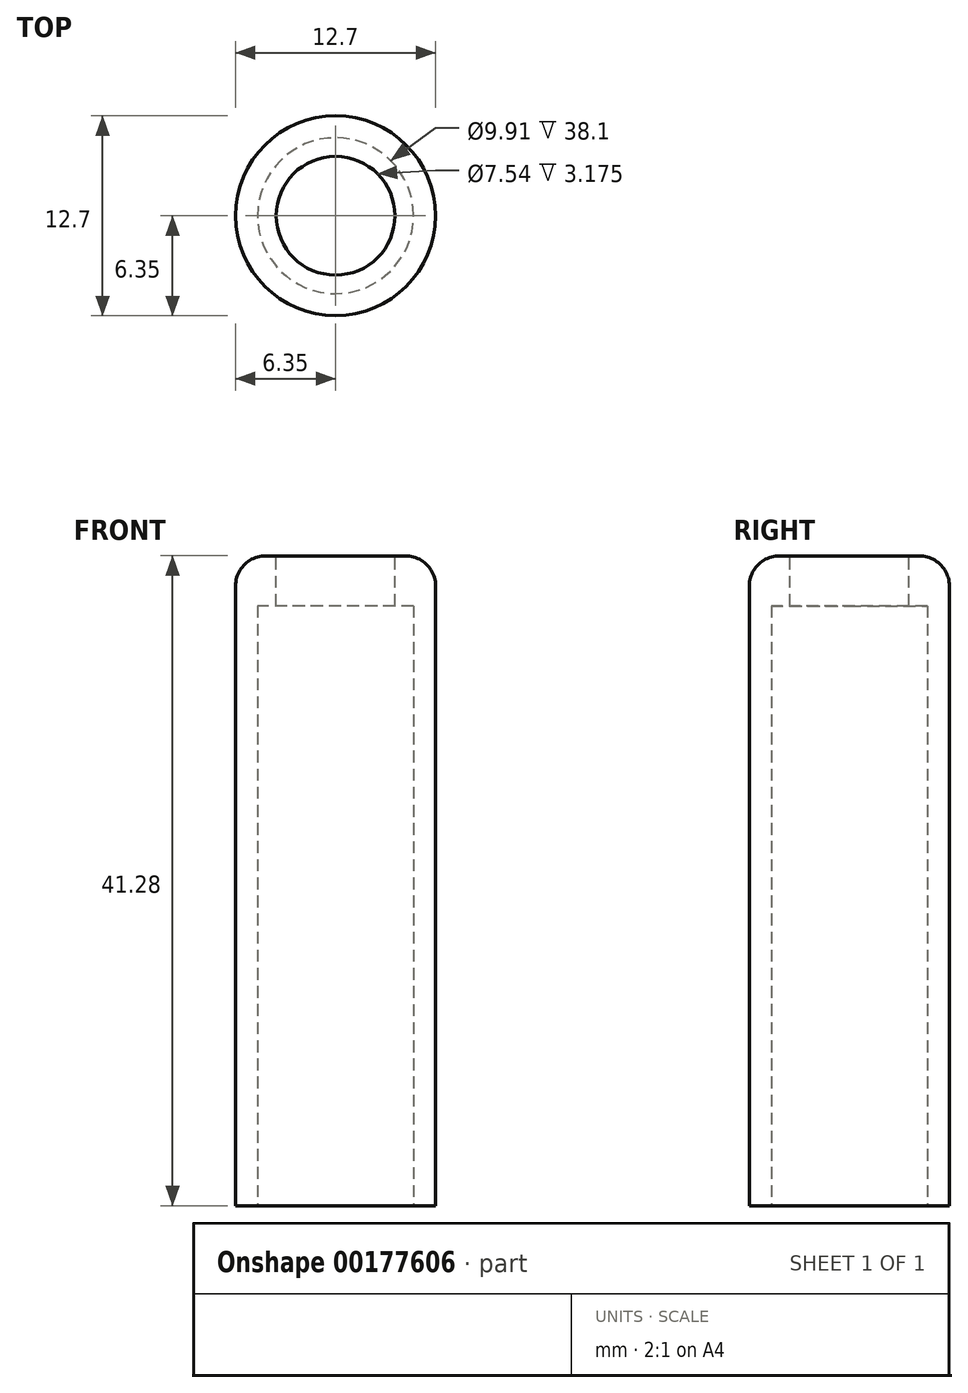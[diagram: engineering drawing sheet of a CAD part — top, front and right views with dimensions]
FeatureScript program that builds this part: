
annotation { "Feature Type Name" : "Feature", "Feature Type Description" : "" }
export const myFeature = defineFeature(function(context is Context, id is Id, definition is map)
    precondition{}
    {
        {
            var Q0;
            Q0=qCreatedBy(makeId("Top.planeOp"),FACE);
            var sketch = newSketch(context, id + "F0", { "sketchPlane" : qUnion([Q0])});
            skCircle(sketch, "E0", {"center": v(0, 0) * mm, "radius": 6.35 * mm});
            skSolve(sketch);
        }
        {
            var Q0;
            Q0=makeQuery(id+"F0.imprint","IMPRINT",FACE,{"disambiguationData":[TD([[makeQuery(id+"F0.imprint","IMPRINT",EDGE,{"derivedFrom":sQuery(id+"F0.wireOp",EDGE,"E0")}),1.0]])]});
            extrude(context, id + "F1", {"entities" : qUnion([Q0]), "depth" : 41.27 * mm});
        }
        {
            var Q0;
            Q0=qCreatedBy(makeId("Top.planeOp"),FACE);
            var sketch = newSketch(context, id + "F2", { "sketchPlane" : qUnion([Q0])});
            skCircle(sketch, "E1", {"center": v(0, 0) * mm, "radius": 4.95 * mm});
            skSolve(sketch);
        }
        {
            var Q0;
            Q0 = qSketchRegion(id + "F2", true);
            extrude(context, id + "F3", {"entities" : qUnion([Q0]), "operationType" : NewBodyOperationType.REMOVE, "depth" : 38.1 * mm});
        }
        {
            var Q0;
            Q0=makeQuery(id+"F1.opExtrude","CAP_FACE",FACE,{"disambiguationData":[OSD([sQuery(id+"F0.wireOp",EDGE,"E0")])],"isStart":false});
            cPlane(context, id + "F4", {"entities" : qUnion([Q0]), "cplaneType" : CPlaneType.OFFSET, "offset" : 0 * mm, "width" : 152.4 * mm, "height" : 152.4 * mm});
        }
        {
            var Q0;
            Q0=qCreatedBy(id+"F4.planeOp",FACE);
            var sketch = newSketch(context, id + "F5", { "sketchPlane" : qUnion([Q0])});
            skCircle(sketch, "E2", {"center": v(0, 0) * mm, "radius": 3.77 * mm});
            skSolve(sketch);
        }
        {
            var Q0;
            Q0=makeQuery(id+"F5.imprint","IMPRINT",FACE,{"disambiguationData":[TD([[makeQuery(id+"F5.imprint","IMPRINT",EDGE,{"derivedFrom":sQuery(id+"F5.wireOp",EDGE,"E2")}),1.0]])]});
            extrude(context, id + "F6", {"entities" : qUnion([Q0]), "operationType" : NewBodyOperationType.REMOVE, "endBound" : BoundingType.UP_TO_NEXT, "oppositeDirection" : true, "depth" : 25.4 * mm});
        }
        {
            var Q0;
            Q0=makeQuery(id+"F1.opExtrude","CAP_EDGE",EDGE,{"disambiguationData":[OSD([sQuery(id+"F0.wireOp",EDGE,"E0")])],"isStart":false});
            fillet(context, id + "F7", {"entities" : qUnion([Q0]), "radius" : 1.9 * mm, "tangentPropagation" : true, "allowEdgeOverflow" : false});
        }
    });
